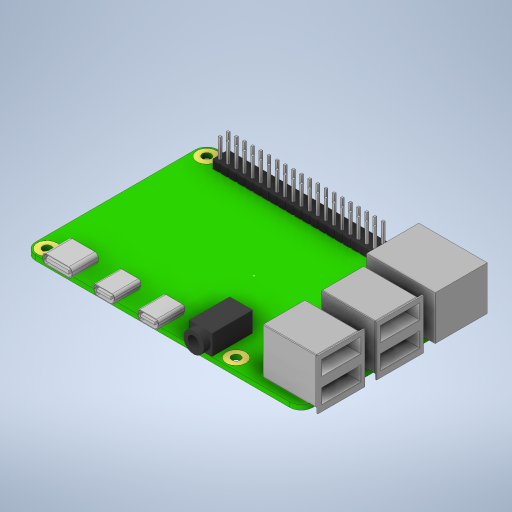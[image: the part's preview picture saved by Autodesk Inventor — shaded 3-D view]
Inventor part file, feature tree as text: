
AUTODESK INVENTOR PART (.ipt)
format: ipt  version: 2023.1 (Build 271208000, 208)  size: 1,241,088 bytes
history: native  units: mm
features: extrude x18, sketch x13, projected_geometry x4, pattern_linear x3, fillet x2, other x1, chamfer x1
ambient origin geometry x8: Origin, YZ Plane, XZ Plane, XY Plane, X Axis, Y Axis, Z Axis, Center Point
bodies: Body1 (feature_tree)
feature tree (42):
  other  "솔리드1"
  sketch  "스케치1"
  extrude  "돌출1"  Depth=85.0mm
  extrude  "돌출2"  Depth=56.0mm
  sketch  "스케치2"
  extrude  "돌출3"  Depth=2.7mm
  extrude  "돌출4"  Depth=6.0mm
  extrude  "돌출5"  Depth=3.5mm
  fillet  "모깎기1"  Radius=3.5mm
  fillet  "모깎기2"  Radius=3.5mm
  extrude  "돌출6"  Depth=20.0mm
  sketch  "스케치5"
  extrude  "돌출7"  Depth=3.5mm
  extrude  "돌출8"  Depth=1.5mm TaperAngle=0.0deg
  extrude  "돌출9"  Depth=1.51mm TaperAngle=0.0deg
  sketch  "스케치7"
  extrude  "돌출10"  Depth=45.75mm
  extrude  "돌출11"  Depth=27.0mm
  pattern_linear  "직사각형 패턴1"  Spacing1=9.0mm  [1 undecoded]
  extrude  "돌출12"  Depth=16.0mm
  extrude  "돌출13"  Depth=21.0mm
  chamfer  "모따기1"  Distance=13.0mm
  pattern_linear  "직사각형 패턴2"  Spacing1=17.5mm  [1 undecoded]
  sketch  "스케치10"
  sketch  "스케치11"
  extrude  "돌출14"  Depth=13.0mm
  extrude  "돌출15"  Depth=17.5mm
  extrude  "돌출16"  Depth=3.3mm
  extrude  "돌출17"  Depth=13.5mm TaperAngle=0.0deg
  extrude  "돌출18"  Depth=14.0mm TaperAngle=0.0deg
  pattern_linear  "직사각형 패턴3"  Spacing1=0.7mm  [1 undecoded]
  sketch  "스케치3"
  projected_geometry  "투영된 루프1"
  projected_geometry  "투영된 루프2"
  sketch  "스케치4"
  sketch  "스케치6"
  projected_geometry  "투영된 루프3"
  sketch  "스케치8"
  sketch  "스케치9"
  projected_geometry  "투영된 루프4"
  sketch  "스케치12"
  sketch  "스케치14"
note: 3 required parameter values undecoded (feature->parameter linkage not recoverable at this tier; creation-order binding heuristic only, values carry confidence <= 0.55)
